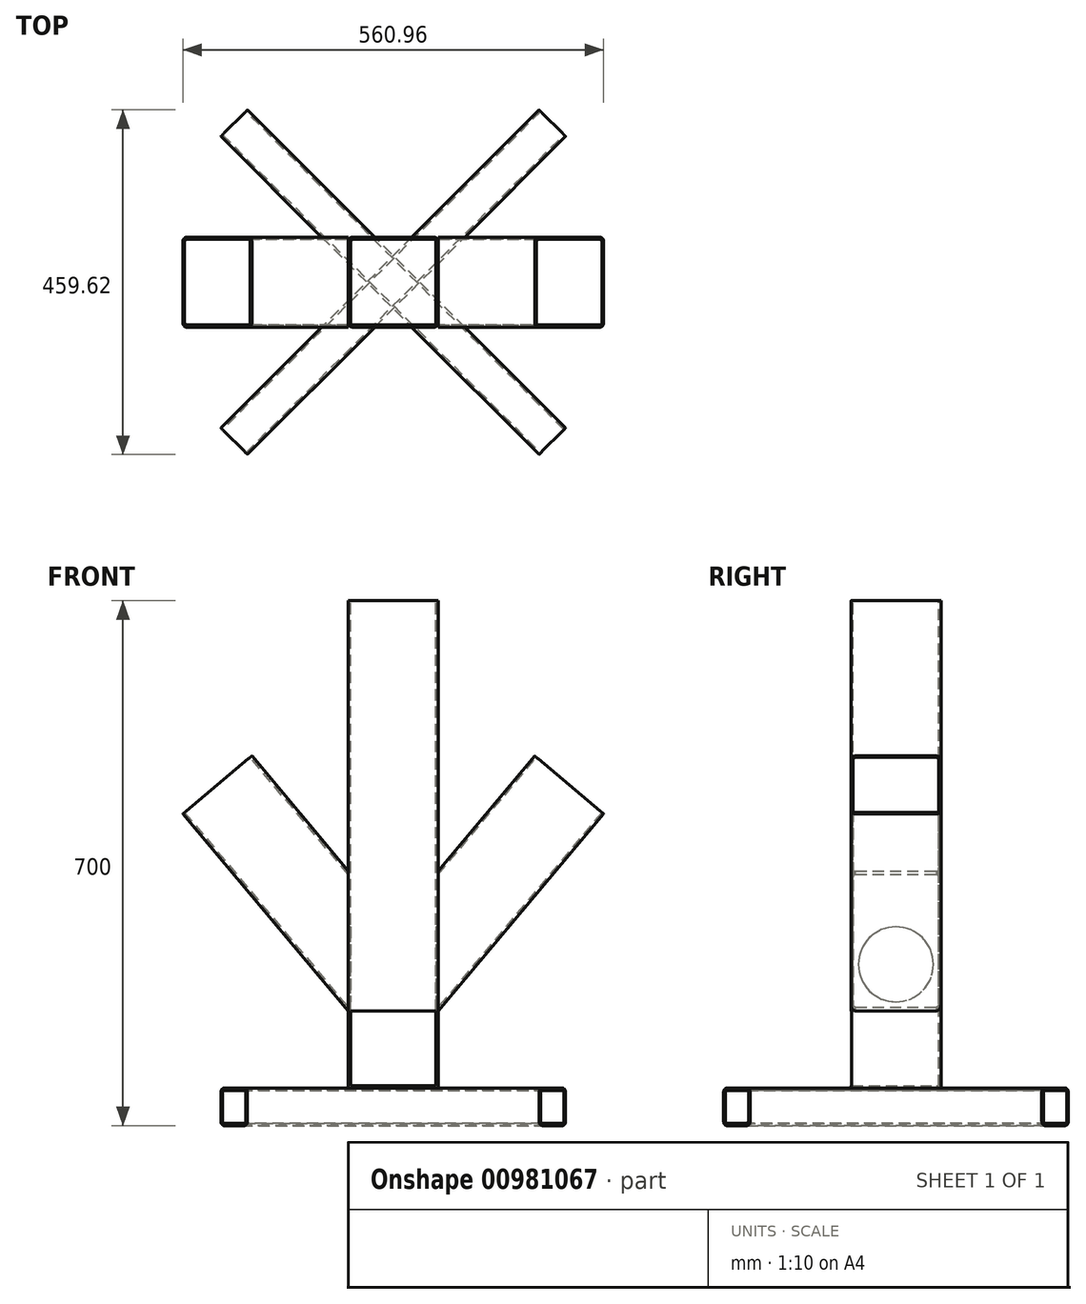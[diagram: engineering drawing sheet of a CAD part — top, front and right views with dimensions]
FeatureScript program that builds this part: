
annotation { "Feature Type Name" : "Feature", "Feature Type Description" : "" }
export const myFeature = defineFeature(function(context is Context, id is Id, definition is map)
    precondition{}
    {
        {
            var Q0;
            Q0=qCreatedBy(makeId("Front.planeOp"),FACE);
            var sketch = newSketch(context, id + "F0", { "sketchPlane" : qUnion([Q0])});
            skLineSegment(sketch, "E0.bottom", {"start": v(-60, 0) * mm, "end": v(60, 0) * mm});
            skLineSegment(sketch, "E0.top", {"start": v(-60, 650) * mm, "end": v(60, 650) * mm});
            skLineSegment(sketch, "E0.left", {"start": v(-60, 0) * mm, "end": v(-60, 650) * mm});
            skLineSegment(sketch, "E0.right", {"start": v(60, 0) * mm, "end": v(60, 650) * mm});
            skSolve(sketch);
        }
        {
            var Q0;
            Q0=makeQuery(id+"F0.imprint","IMPRINT",FACE,{"disambiguationData":[TD([[makeQuery(id+"F0.imprint","IMPRINT",EDGE,{"derivedFrom":sQuery(id+"F0.wireOp",EDGE,"E0.bottom")}),1.0]])]});
            extrude(context, id + "F1", {"entities" : qUnion([Q0]), "depth" : 60 * mm, "offsetDistance" : 25 * mm, "hasSecondDirection" : true, "secondDirectionOppositeDirection" : true, "secondDirectionDepth" : 60 * mm});
        }
        {
            var Q0;
            Q0=makeQuery(id+"F1.opExtrude","CAP_EDGE",EDGE,{"disambiguationData":[OSD([sQuery(id+"F0.wireOp",EDGE,"E0.right")])],"isStart":false});
            var Q1;
            Q1=makeQuery(id+"F1.opExtrude","CAP_EDGE",EDGE,{"disambiguationData":[OSD([sQuery(id+"F0.wireOp",EDGE,"E0.left")])],"isStart":false});
            var Q2;
            Q2=makeQuery(id+"F1.opExtrude","CAP_EDGE",EDGE,{"disambiguationData":[OSD([sQuery(id+"F0.wireOp",EDGE,"E0.right")])],"isStart":true});
            var Q3;
            Q3=makeQuery(id+"F1.opExtrude","CAP_EDGE",EDGE,{"disambiguationData":[OSD([sQuery(id+"F0.wireOp",EDGE,"E0.left")])],"isStart":true});
            fillet(context, id + "F2", {"entities" : qUnion([Q0, Q1, Q2, Q3]), "radius" : 6 * mm, "tangentPropagation" : true, "allowEdgeOverflow" : false});
        }
        {
            var Q0;
            Q0=makeQuery(id+"F1.opExtrude","SWEPT_FACE",FACE,{"disambiguationData":[OSD([sQuery(id+"F0.wireOp",EDGE,"E0.top")])]});
            shell(context, id + "F3", {"entities" : qUnion([Q0]), "thickness" : 3 * mm});
        }
        {
            var Q0;
            Q0=makeQuery(id+"F1.opExtrude","CAP_FACE",FACE,{"disambiguationData":[OSD([sQuery(id+"F0.wireOp",EDGE,"E0.bottom"),sQuery(id+"F0.wireOp",EDGE,"E0.top"),sQuery(id+"F0.wireOp",EDGE,"E0.left"),sQuery(id+"F0.wireOp",EDGE,"E0.right")])],"isStart":false});
            var sketch = newSketch(context, id + "F4", { "sketchPlane" : qUnion([Q0])});
            skLineSegment(sketch, "E1.bottom", {"start": v(-57, 3) * mm, "end": v(57, 3) * mm});
            skLineSegment(sketch, "E1.top", {"start": v(-57, 103) * mm, "end": v(57, 103) * mm});
            skLineSegment(sketch, "E1.left", {"start": v(-57, 3) * mm, "end": v(-57, 103) * mm});
            skLineSegment(sketch, "E1.right", {"start": v(57, 3) * mm, "end": v(57, 103) * mm});
            skSolve(sketch);
        }
        {
            var Q0;
            {var subQ0=sQuery(id+"F4.wireOp",EDGE,"E1.left");Q0=makeQuery(id+"F4.imprint","IMPRINT",FACE,{"disambiguationData":[TD([[makeQuery(id+"F4.imprint","IMPRINT",EDGE,{"derivedFrom":subQ0}),-1.0]])]});}
            var Q1;
            {var subQ0=sQuery(id+"F4.wireOp",EDGE,"E1.bottom");var subQ1=sQuery(id+"F0.wireOp",EDGE,"E0.right");var subQ2=sQuery(id+"F0.wireOp",EDGE,"E0.left");var subQ3=makeQuery(id+"F1.opExtrude","CAP_FACE",FACE,{"disambiguationData":[OSD([sQuery(id+"F0.wireOp",EDGE,"E0.bottom"),sQuery(id+"F0.wireOp",EDGE,"E0.top"),subQ2,subQ1])],"isStart":false});var subQ4=makeQuery(id+"F2.opFillet","BLEND_EDGE",EDGE,{"blendedFrom":[makeQuery(id+"F1.opExtrude","CAP_EDGE",EDGE,{"disambiguationData":[OSD([subQ2])],"isStart":false}),subQ3],"blendedInto":[subQ3]});var subQ5=makeQuery(id+"F4.imprint","INTERSECT",VERTEX,{"derivedFrom":[subQ4,subQ0]});Q1=makeQuery(id+"F4.imprint","IMPRINT",FACE,{"disambiguationData":[TD([[makeQuery(id+"F4.imprint","IMPRINT",EDGE,{"disambiguationData":[TD([[subQ5,-1.0]])],"derivedFrom":subQ0}),1.0]])]});}
            var Q2;
            {var subQ0=sQuery(id+"F4.wireOp",EDGE,"E1.right");Q2=makeQuery(id+"F4.imprint","IMPRINT",FACE,{"disambiguationData":[TD([[makeQuery(id+"F4.imprint","IMPRINT",EDGE,{"derivedFrom":subQ0}),1.0]])]});}
            extrude(context, id + "F5", {"entities" : qUnion([Q0, Q1, Q2]), "operationType" : NewBodyOperationType.REMOVE, "endBound" : BoundingType.UP_TO_NEXT, "oppositeDirection" : true, "depth" : 25 * mm, "offsetDistance" : 25 * mm});
        }
        {
            var Q0;
            Q0=makeQuery(id+"F1.opExtrude","SWEPT_FACE",FACE,{"disambiguationData":[OSD([sQuery(id+"F0.wireOp",EDGE,"E0.right")])]});
            var sketch = newSketch(context, id + "F6", { "sketchPlane" : qUnion([Q0])});
            skCircle(sketch, "E2", {"center": v(0, 165) * mm, "radius": 50 * mm});
            skSolve(sketch);
        }
        {
            var Q0;
            Q0=makeQuery(id+"F6.imprint","IMPRINT",FACE,{"disambiguationData":[TD([[makeQuery(id+"F6.imprint","IMPRINT",EDGE,{"derivedFrom":sQuery(id+"F6.wireOp",EDGE,"E2")}),1.0]])]});
            extrude(context, id + "F7", {"entities" : qUnion([Q0]), "operationType" : NewBodyOperationType.REMOVE, "endBound" : BoundingType.THROUGH_ALL, "oppositeDirection" : true, "depth" : 25 * mm, "offsetDistance" : 25 * mm});
        }
        {
            var Q0;
            Q0=qCreatedBy(makeId("Front.planeOp"),FACE);
            var sketch = newSketch(context, id + "F8", { "sketchPlane" : qUnion([Q0])});
            skLineSegment(sketch, "E3", {"start": v(60, 103) * mm, "end": v(60, 289.69) * mm});
            skLineSegment(sketch, "E4", {"start": v(60, 289.69) * mm, "end": v(188.56, 442.9) * mm});
            skLineSegment(sketch, "E5", {"start": v(188.56, 442.9) * mm, "end": v(280.48, 365.76) * mm});
            skLineSegment(sketch, "E6", {"start": v(280.48, 365.76) * mm, "end": v(60, 103) * mm});
            skSolve(sketch);
        }
        {
            var Q0;
            Q0=makeQuery(id+"F8.imprint","IMPRINT",FACE,{"disambiguationData":[TD([[makeQuery(id+"F8.imprint","IMPRINT",EDGE,{"derivedFrom":sQuery(id+"F8.wireOp",EDGE,"E3")}),-1.0]])]});
            extrude(context, id + "F9", {"entities" : qUnion([Q0]), "depth" : 60 * mm, "offsetDistance" : 25 * mm, "hasSecondDirection" : true, "secondDirectionOppositeDirection" : true, "secondDirectionDepth" : 60 * mm});
        }
        {
            var Q0;
            Q0=makeQuery(id+"F9.opExtrude","CAP_EDGE",EDGE,{"disambiguationData":[OSD([sQuery(id+"F8.wireOp",EDGE,"E4")])],"isStart":false});
            var Q1;
            Q1=makeQuery(id+"F9.opExtrude","CAP_EDGE",EDGE,{"disambiguationData":[OSD([sQuery(id+"F8.wireOp",EDGE,"E4")])],"isStart":true});
            var Q2;
            Q2=makeQuery(id+"F9.opExtrude","CAP_EDGE",EDGE,{"disambiguationData":[OSD([sQuery(id+"F8.wireOp",EDGE,"E6")])],"isStart":false});
            var Q3;
            Q3=makeQuery(id+"F9.opExtrude","CAP_EDGE",EDGE,{"disambiguationData":[OSD([sQuery(id+"F8.wireOp",EDGE,"E6")])],"isStart":true});
            fillet(context, id + "F10", {"entities" : qUnion([Q0, Q1, Q2, Q3]), "radius" : 6 * mm, "tangentPropagation" : true, "allowEdgeOverflow" : false});
        }
        {
            var Q0;
            Q0=makeQuery(id+"F9.opExtrude","SWEPT_FACE",FACE,{"disambiguationData":[OSD([sQuery(id+"F8.wireOp",EDGE,"E5")])]});
            var Q1;
            Q1=makeQuery(id+"F9.opExtrude","SWEPT_FACE",FACE,{"disambiguationData":[OSD([sQuery(id+"F8.wireOp",EDGE,"E3")])]});
            shell(context, id + "F11", {"entities" : qUnion([Q0, Q1]), "thickness" : 3 * mm});
        }
        {
            var Q0;
            Q0=makeQuery(id+"F9.opExtrude","SWEPT_BODY",BODY,{"disambiguationData":[OSD([sQuery(id+"F8.wireOp",EDGE,"E3"),sQuery(id+"F8.wireOp",EDGE,"E4"),sQuery(id+"F8.wireOp",EDGE,"E5"),sQuery(id+"F8.wireOp",EDGE,"E6")])]});
            var Q1;
            Q1=qCreatedBy(makeId("Right.planeOp"),FACE);
            mirror(context, id + "F12", {"operationType" : NewBodyOperationType.ADD, "entities" : qUnion([Q0]), "mirrorPlane" : qUnion([Q1])});
        }
        {
            var Q0;
            Q0=qCreatedBy(makeId("Top.planeOp"),FACE);
            var sketch = newSketch(context, id + "F13", { "sketchPlane" : qUnion([Q0])});
            skLineSegment(sketch, "E7", {"start": v(-194.45, -229.8) * mm, "end": v(229.8, 194.45) * mm});
            skLineSegment(sketch, "E8", {"start": v(229.8, 194.45) * mm, "end": v(194.45, 229.8) * mm});
            skLineSegment(sketch, "E9", {"start": v(194.45, 229.8) * mm, "end": v(-229.8, -194.45) * mm});
            skLineSegment(sketch, "E10", {"start": v(-229.8, -194.45) * mm, "end": v(-194.45, -229.8) * mm});
            skLineSegment(sketch, "E11", {"start": v(212.13, 212.13) * mm, "end": v(-212.13, -212.13) * mm});
            skLineSegment(sketch, "E12", {"start": v(-212.13, -212.13) * mm, "end": v(-22.29, -22.29) * mm});
            skSolve(sketch);
        }
        {
            var Q0;
            {var subQ2=sQuery(id+"F13.wireOp",EDGE,"E9");Q0=makeQuery(id+"F13.imprint","IMPRINT",FACE,{"disambiguationData":[TD([[makeQuery(id+"F13.imprint","IMPRINT",EDGE,{"derivedFrom":subQ2}),1.0]])]});}
            var Q1;
            {var subQ2=sQuery(id+"F13.wireOp",EDGE,"E7");Q1=makeQuery(id+"F13.imprint","IMPRINT",FACE,{"disambiguationData":[TD([[makeQuery(id+"F13.imprint","IMPRINT",EDGE,{"derivedFrom":subQ2}),1.0]])]});}
            extrude(context, id + "F14", {"entities" : qUnion([Q0, Q1]), "oppositeDirection" : true, "depth" : 50 * mm, "offsetDistance" : 25 * mm});
        }
        {
            var Q0;
            Q0=makeQuery(id+"F14.opExtrude","CAP_EDGE",EDGE,{"disambiguationData":[OSD([sQuery(id+"F13.wireOp",EDGE,"E7")])],"isStart":true});
            var Q1;
            Q1=makeQuery(id+"F14.opExtrude","CAP_EDGE",EDGE,{"disambiguationData":[OSD([sQuery(id+"F13.wireOp",EDGE,"E9")])],"isStart":true});
            var Q2;
            Q2=makeQuery(id+"F14.opExtrude","CAP_EDGE",EDGE,{"disambiguationData":[OSD([sQuery(id+"F13.wireOp",EDGE,"E7")])],"isStart":false});
            var Q3;
            Q3=makeQuery(id+"F14.opExtrude","CAP_EDGE",EDGE,{"disambiguationData":[OSD([sQuery(id+"F13.wireOp",EDGE,"E9")])],"isStart":false});
            fillet(context, id + "F15", {"entities" : qUnion([Q0, Q1, Q2, Q3]), "radius" : 6 * mm, "tangentPropagation" : true, "allowEdgeOverflow" : false});
        }
        {
            var Q0;
            Q0=makeQuery(id+"F14.opExtrude","SWEPT_FACE",FACE,{"disambiguationData":[OSD([sQuery(id+"F13.wireOp",EDGE,"E10")])]});
            var Q1;
            Q1=makeQuery(id+"F14.opExtrude","SWEPT_FACE",FACE,{"disambiguationData":[OSD([sQuery(id+"F13.wireOp",EDGE,"E8")])]});
            shell(context, id + "F16", {"entities" : qUnion([Q0, Q1]), "thickness" : 3 * mm});
        }
        {
            var Q0;
            Q0=qCreatedBy(makeId("Front.planeOp"),FACE);
            var sketch = newSketch(context, id + "F17", { "sketchPlane" : qUnion([Q0])});
            skLineSegment(sketch, "E13", {"start": v(0, 0) * mm, "end": v(0, 355.2) * mm});
            skSolve(sketch);
        }
        {
            var Q0;
            Q0=makeQuery(id+"F14.opExtrude","SWEPT_BODY",BODY,{"disambiguationData":[OSD([sQuery(id+"F13.wireOp",EDGE,"E7"),sQuery(id+"F13.wireOp",EDGE,"E8"),sQuery(id+"F13.wireOp",EDGE,"E9"),sQuery(id+"F13.wireOp",EDGE,"E10")])]});
            var Q1;
            Q1=sQuery(id+"F17.wireOp",EDGE,"E13");
            circularPattern(context, id + "F18", {"entities" : qUnion([Q0]), "axis" : qUnion([Q1]), "angle" : 90 * degree, "instanceCount" : 2, "equalSpace" : true});
        }
    });
